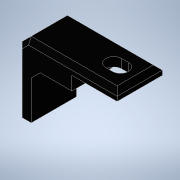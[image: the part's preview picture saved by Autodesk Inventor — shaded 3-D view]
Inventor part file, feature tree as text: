
AUTODESK INVENTOR PART (.ipt)
format: ipt  version: 2021 (Build 250183000, 183)  size: 296,448 bytes
history: native  units: mm
features: chamfer x3, extrude x2, sketch x2
ambient origin geometry x8: Origin, YZ Plane, XZ Plane, XY Plane, X Axis, Y Axis, Z Axis, Center Point
bodies: Solid1 (feature_tree)
feature tree (7):
  extrude  "Extrusion1"  Depth=10.0mm
  chamfer  "Chamfer1"  Distance=9.0mm
  extrude  "Extrusion2"  Depth=3.0mm
  chamfer  "Chamfer2"  Distance=10.6mm
  chamfer  "Chamfer3"  Distance=10.0mm
  sketch  "Sketch1"  dims[d0=2.0mm d1=10.0mm]
  sketch  "Sketch2"  dims[d2=3.0mm d3=9.0mm d4=3.0mm d5=10.6mm d6=10.0mm d7=0.0mm d8=2.0mm d9=2.0mm d10=45.0deg d11=1.75mm d12=1.5mm d13=5.0mm d14=0.0mm d15=0.0mm d16=2.0mm d17=2.0mm d18=45.0deg d19=1.0mm d20=2.0mm d21=45.0deg]
